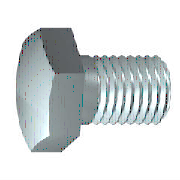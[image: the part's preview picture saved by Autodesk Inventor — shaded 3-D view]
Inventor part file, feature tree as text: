
AUTODESK INVENTOR PART (.ipt)
format: ipt  version: 2025 (Build 290162010, 162A)  size: 211,968 bytes
history: native  units: mm (DEFAULTED — no unit token found)
features: other x3, revolve x2, extrude x2, sketch x2, fillet x1
ambient origin geometry x8: Origin, YZ Plane, XZ Plane, XY Plane, X Axis, Y Axis, Z Axis, Center Point
bodies: Solid1 (feature_tree)
feature tree (10):
  revolve  "Revolution1"  Angle=45.0deg
  extrude  "Extrusion1"  TaperAngle=60.0deg  [1 undecoded]
  revolve  "Revolution2"  [1 undecoded]
  extrude  "Extrusion2"  TaperAngle=30.0deg  [1 undecoded]
  other  "MSC_A1"
  other  "MSC_PF1"
  other  "MSC_PT1"
  fillet  "Fillet1"  [1 undecoded]
  sketch  "Sketch2"  dims[d3=30.0deg d5=45.0deg]
  sketch  "Sketch4"  dims[d8=90.0deg d9=60.0deg d13=0.0mm d14=30.0deg d16=90.0deg d18=0.0mm d22=0.0mm d23=0.0mm d25=0.0mm d26=0.0mm d27=12.0mm d28=1.28mm d29=0.0mm d30=0.4mm d31=0.0mm]
note: 4 required parameter values undecoded (feature->parameter linkage not recoverable at this tier; creation-order binding heuristic only, values carry confidence <= 0.55)